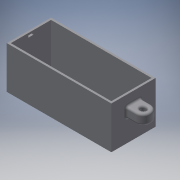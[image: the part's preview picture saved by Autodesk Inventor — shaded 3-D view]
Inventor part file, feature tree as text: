
AUTODESK INVENTOR PART (.ipt)
format: ipt  version: 2019 (Build 230136000, 136)  size: 196,608 bytes
history: native  units: mm
features: sketch x7, extrude x6, hole x1, fillet x1, projected_geometry x1
ambient origin geometry x8: Origin, YZ Plane, XZ Plane, XY Plane, X Axis, Y Axis, Z Axis, Center Point
bodies: Solid1 (feature_tree)
feature tree (16):
  extrude  "Extrusion1"  Depth=2.0mm
  extrude  "Extrusion2"  Depth=5.0mm
  extrude  "Extrusion3"  Depth=2.0mm
  extrude  "Extrusion4"  TaperAngle=0.0deg  [1 undecoded]
  extrude  "Extrusion5"  Depth=15.0mm
  hole  "Hole1"  [1 undecoded]
  fillet  "Fillet1"  Radius=10.0mm
  extrude  "Extrusion6"  Depth=2.0mm
  sketch  "Sketch1"  dims[d4=0.0mm d5=2.0mm]
  sketch  "Sketch2"  dims[d6=0.0mm d7=5.0mm]
  sketch  "Sketch3"  dims[d8=2.0mm d9=2.0mm]
  sketch  "Sketch4"  dims[d10=2.0mm d11=0.0mm]
  sketch  "Sketch5"  dims[d12=10.0mm d13=15.0mm]
  projected_geometry  "Projected Loop1"
  sketch  "Sketch6"  dims[d14=2.0mm d15=10.0mm d16=0.0mm d17=10.0mm d18=0.0mm]
  sketch  "Sketch7"  dims[d19=5.5mm d20=6.0mm d21=10.4mm d22=2.0mm d23=90.0deg d24=8.0mm d25=20.594885mm d26=2.0mm d27=8.0mm d28=3.5mm d29=0.0mm]
note: 2 required parameter values undecoded (feature->parameter linkage not recoverable at this tier; creation-order binding heuristic only, values carry confidence <= 0.55)
